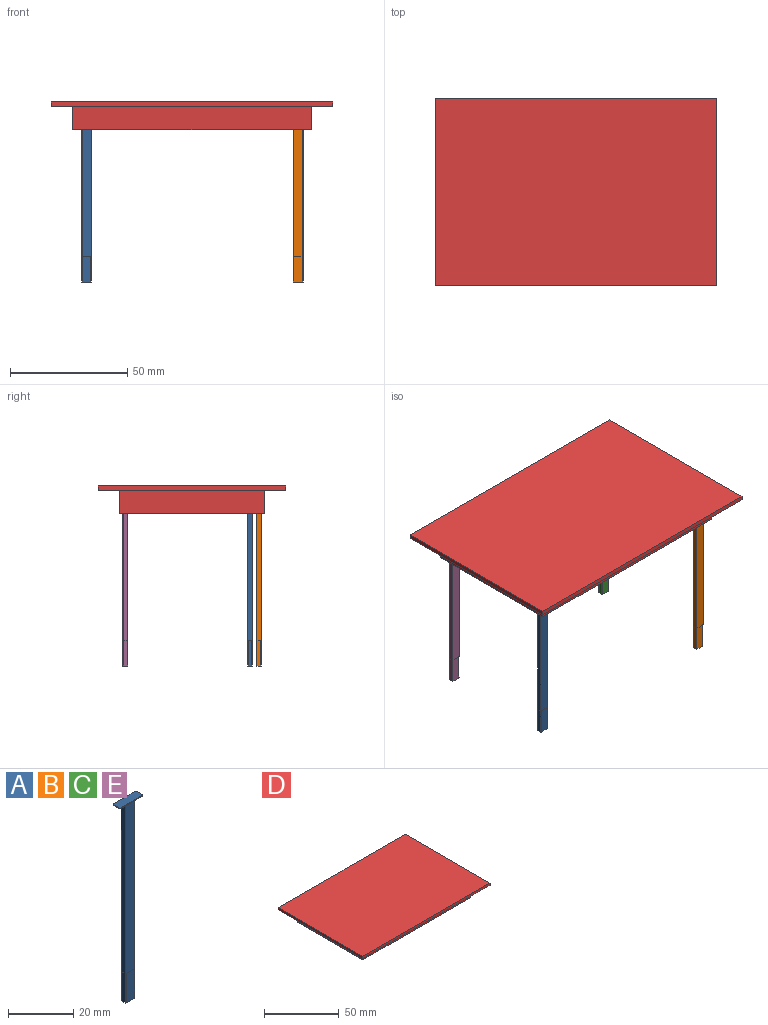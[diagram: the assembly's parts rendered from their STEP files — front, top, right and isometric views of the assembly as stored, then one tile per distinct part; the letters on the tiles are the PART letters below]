
ASSEMBLY  parts=5 mates=4
PART A: 35 faces, bbox 10x3.1x74.9 mm
  f0: plane 11.01x1.62mm, normal (1,0,0), area 17.7mm2, adj f4,f5,f8,f13
  f1: plane 11.01x3.62mm, normal (0,1,0), area 39.7mm2, adj f4,f5,f6,f14
  f2: plane 11.01x1.62mm, normal (-1,0,0), area 17.7mm2, adj f4,f6,f7,f15
  f3: plane 11.01x3.62mm, normal (0,-1,0), area 39.7mm2, adj f4,f7,f8,f12
  f4: plane 4.01x2.01mm, normal (0,0,-1), area 8mm2, adj f0,f1,f2,f3,f5,f6,f7,f8
  f5: cylinder r=0.2mm len=11mm, axis (0,0,-1), area 3.5mm2, adj f0,f1,f4,f9
  f6: cylinder r=0.2mm len=11mm, axis (0,0,1), area 3.5mm2, adj f1,f2,f4,f10
  f7: cylinder r=0.2mm len=11mm, axis (0,0,-1), area 3.5mm2, adj f2,f3,f4,f11
  f8: cylinder r=0.2mm len=11mm, axis (0,0,1), area 3.5mm2, adj f0,f3,f4,f16
  f9: plane 0.21x0.21mm, normal (0,0,-1), area 0mm2, adj f5,f13,f14
  f10: plane 0.21x0.21mm, normal (0,0,-1), area 0mm2, adj f6,f14,f15
  f11: plane 0.21x0.21mm, normal (0,0,-1), area 0mm2, adj f7,f12,f15
  f12: plane 63.51x4.01mm, normal (0,-1,0), area 254mm2, adj f3,f11,f13,f15,f16,f22
  f13: plane 63.51x2.01mm, normal (1,0,0), area 127mm2, adj f0,f9,f12,f14,f16,f22
  f14: plane 63.51x4.01mm, normal (0,1,0), area 254mm2, adj f1,f9,f10,f13,f15,f22
  f15: plane 63.51x2.01mm, normal (-1,0,0), area 127mm2, adj f2,f10,f11,f12,f14,f22
  f16: plane 0.21x0.21mm, normal (0,0,-1), area 0mm2, adj f8,f12,f13
  f17: plane 2.7x0.2mm, normal (1,0,0), area 0.5mm2, adj f21,f28,f32,f34
  f18: plane 9.6x0.2mm, normal (0,1,0), area 1.9mm2, adj f21,f25,f31,f34
  f19: plane 2.7x0.2mm, normal (-1,0,0), area 0.5mm2, adj f21,f23,f25,f26
  f20: plane 9.6x0.2mm, normal (0,-1,0), area 1.9mm2, adj f21,f23,f27,f28
  f21: plane 10x3.1mm, normal (0,0,1), area 31mm2, adj f17,f18,f19,f20,f23,f25,f28,f34
  f22: plane 9.6x2.7mm, normal (0,0,-1), area 17.9mm2, adj f12,f13,f14,f15,f26,f27,f31,f32
  f23: cylinder r=0.2mm len=0.2mm, axis (0,0,-1), area 0.1mm2, adj f19,f20,f21,f24
  f24: sphere r=0.2mm, area 0.1mm2, adj f23,f26,f27
  f25: cylinder r=0.2mm len=0.2mm, axis (0,0,1), area 0.1mm2, adj f18,f19,f21,f29
  f26: cylinder r=0.2mm len=2.7mm, axis (0,-1,0), area 0.8mm2, adj f19,f22,f24,f29
  f27: cylinder r=0.2mm len=9.6mm, axis (1,0,0), area 3mm2, adj f20,f22,f24,f30
  f28: cylinder r=0.2mm len=0.2mm, axis (0,0,1), area 0.1mm2, adj f17,f20,f21,f30
  f29: sphere r=0.2mm, area 0.1mm2, adj f25,f26,f31
  f30: sphere r=0.2mm, area 0.1mm2, adj f27,f28,f32
  f31: cylinder r=0.2mm len=9.6mm, axis (-1,0,0), area 3mm2, adj f18,f22,f29,f33
  f32: cylinder r=0.2mm len=2.7mm, axis (0,1,0), area 0.8mm2, adj f17,f22,f30,f33
  f33: sphere r=0.2mm, area 0mm2, adj f31,f32,f34
  f34: cylinder r=0.2mm len=0.2mm, axis (0,0,-1), area 0.1mm2, adj f17,f18,f21,f33
PART B: same geometry as A
PART C: same geometry as A
PART D: 16 faces, bbox 120x80x11.8 mm
  f0: plane 120x80mm, normal (0,0,-1), area 3308.8mm2, adj f1,f2,f3,f4,f6,f7,f8,f9
  f1: plane 120x1.8mm, normal (0,-1,0), area 216mm2, adj f0,f2,f4,f5
  f2: plane 80x1.8mm, normal (1,0,0), area 144mm2, adj f0,f1,f3,f5
  f3: plane 120x1.8mm, normal (0,1,0), area 216mm2, adj f0,f2,f4,f5
  f4: plane 80x1.8mm, normal (-1,0,0), area 144mm2, adj f0,f1,f3,f5
  f5: plane 120x80mm, normal (0,0,1), area 9600mm2, adj f1,f2,f3,f4
  f6: plane 61.8x10mm, normal (1,0,0), area 618mm2, adj f0,f7,f9,f10
  f7: plane 101.8x10mm, normal (0,-1,0), area 1018mm2, adj f0,f6,f8,f10
  f8: plane 61.8x10mm, normal (-1,0,0), area 618mm2, adj f0,f7,f9,f10
  f9: plane 101.8x10mm, normal (0,1,0), area 1018mm2, adj f0,f6,f8,f10
  f10: plane 101.8x61.8mm, normal (0,0,-1), area 291.2mm2, adj f6,f7,f8,f9,f11,f12,f13,f14
  f11: plane 60x10mm, normal (-1,0,0), area 600mm2, adj f10,f12,f14,f15
  f12: plane 100x10mm, normal (0,1,0), area 1000mm2, adj f10,f11,f13,f15
  f13: plane 60x10mm, normal (1,0,0), area 600mm2, adj f10,f12,f14,f15
  f14: plane 100x10mm, normal (0,-1,0), area 1000mm2, adj f10,f11,f13,f15
  f15: plane 100x60mm, normal (0,0,-1), area 6000mm2, adj f11,f12,f13,f14
PART E: same geometry as A
PLACE A t=(-177.27,73.96,187.55)mm
PLACE B t=(-87.36,70.2,187.55)mm
PLACE C t=(-87.07,127.26,187.55)mm
PLACE D t=(-132.42,98.66,262.45)mm
PLACE E t=(-177.46,126.94,187.55)mm
MATE planar B.f21 <-> D.f15  axis (0,0,1) through (-87.36,70.2,262.45)mm
MATE planar C.f21 <-> D.f15  axis (0,0,1) through (-87.07,127.26,262.45)mm
MATE planar E.f21 <-> D.f15  axis (0,0,1) through (-177.46,126.94,262.45)mm
MATE planar A.f34 <-> D.f15  axis (0,0,1) through (-172.47,75.31,262.45)mm
